# Revit family: Curtain Wall Door with mullions
name_source: partatom
category: Doors
revit_build: Autodesk Revit Architecture 2012 (Build: 20110309_2315)
units: mm (PartAtom-declared; Revit-internal decimal feet)

## types (1)
- Curtain Wall Door with mullions
    Frame Depth = 100 mm  [stored 0.328084 ft]
    Frame Offset from Wall center = 100 mm  [stored 0.328084 ft]
    Function = Interior
    Glazing Panel Height = 262.66 mm
    Glazing Panel Width = 174.7 mm
    Height = 2293.6 mm
    Horizontal Mullions = 6
    Mullion Depth = 50 mm  [stored 0.164042 ft]
    Mullion Offset from Frame = 20 mm  [stored 0.0656168 ft]
    Mullion Width = 30 mm  [stored 0.0984252 ft]
    Vertical Mullions = 3
    Width = 988.8 mm
    Width Bottom = 175 mm  [stored 0.574147 ft]
    Width Top = 100 mm  [stored 0.328084 ft]
    Width left and right = 100 mm  [stored 0.328084 ft]

note: [stored X ft] marks values corroborated as IEEE doubles in the binary element streams (Revit-internal decimal feet)

## geometry (parser evidence)
native form markers: Sweep x1
no freeform markers — native parametric forms only
